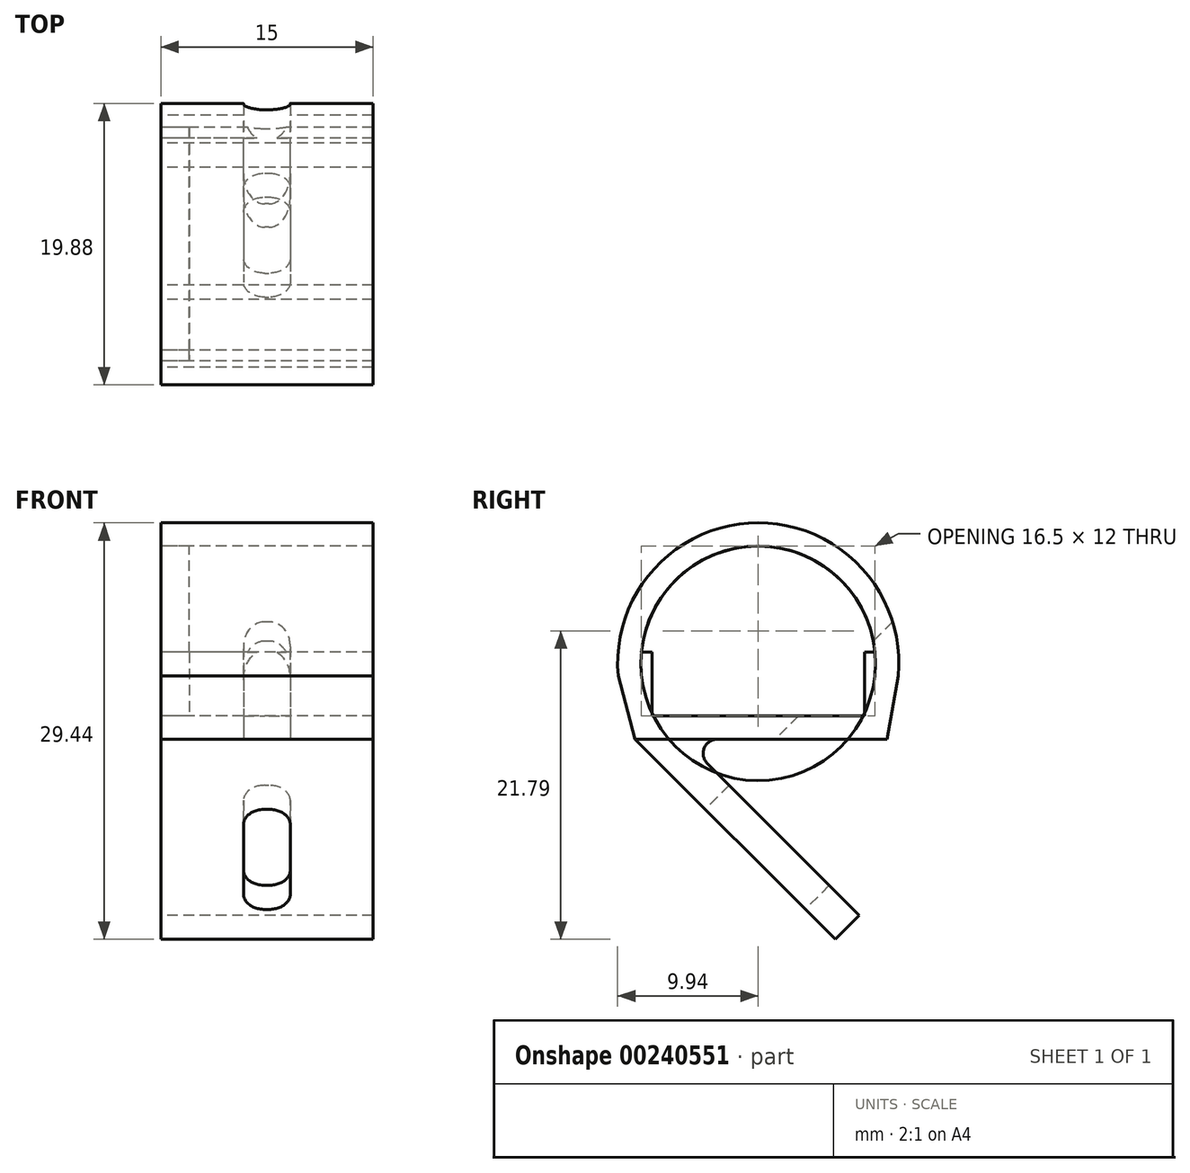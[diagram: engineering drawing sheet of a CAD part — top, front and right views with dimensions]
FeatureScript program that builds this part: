
annotation { "Feature Type Name" : "Feature", "Feature Type Description" : "" }
export const myFeature = defineFeature(function(context is Context, id is Id, definition is map)
    precondition{}
    {
        {
            var Q0;
            Q0=qCreatedBy(makeId("Right.planeOp"),FACE);
            var sketch = newSketch(context, id + "F0", { "sketchPlane" : qUnion([Q0])});
            skLineSegment(sketch, "E0.top", {"start": v(-7.5, -4.5) * mm, "end": v(7.5, -4.5) * mm});
            skLineSegment(sketch, "E0.left", {"start": v(-7.5, 0) * mm, "end": v(-7.5, -4.5) * mm});
            skLineSegment(sketch, "E0.right", {"start": v(7.5, 0) * mm, "end": v(7.5, -4.5) * mm});
            skLineSegment(sketch, "E1", {"start": v(-8.25, 0) * mm, "end": v(-7.5, 0) * mm});
            skArc(sketch, "E2", {"start": v(8.25, 0) * mm, "mid": v(0, 7.5) * mm, "end": v(-8.25, 0) * mm});
            skLineSegment(sketch, "E3", {"start": v(7.5, 0) * mm, "end": v(8.25, 0) * mm});
            skArc(sketch, "E4.3", {"start": v(9.9, -1.68) * mm, "mid": v(0, 9.15) * mm, "end": v(-9.9, -1.68) * mm});
            skLineSegment(sketch, "E4.4", {"start": v(-8.7, -6.15) * mm, "end": v(9.1, -6.15) * mm});
            skLineSegment(sketch, "E5", {"start": v(-9.9, -1.68) * mm, "end": v(-8.7, -6.15) * mm});
            skLineSegment(sketch, "E6", {"start": v(9.9, -1.68) * mm, "end": v(9.1, -6.15) * mm});
            skSolve(sketch);
        }
        {
            var Q0;
            Q0=makeQuery(id+"F0.imprint","IMPRINT",FACE,{"disambiguationData":[TD([[makeQuery(id+"F0.imprint","IMPRINT",EDGE,{"derivedFrom":sQuery(id+"F0.wireOp",EDGE,"E0.top")}),-1.0]])]});
            extrude(context, id + "F1", {"entities" : qUnion([Q0]), "depth" : 15 * mm});
        }
        {
            var Q0;
            Q0=makeQuery(id+"F0.imprint","IMPRINT",FACE,{"disambiguationData":[TD([[makeQuery(id+"F0.imprint","IMPRINT",EDGE,{"derivedFrom":sQuery(id+"F0.wireOp",EDGE,"E0.top")}),1.0]])]});
            extrude(context, id + "F2", {"entities" : qUnion([Q0]), "depth" : 2 * mm});
        }
        {
            var Q0;
            Q0=qCreatedBy(makeId("Right.planeOp"),FACE);
            var sketch = newSketch(context, id + "F3", { "sketchPlane" : qUnion([Q0])});
            skLineSegment(sketch, "E7.0", {"start": v(-2.9, -6.15) * mm, "end": v(9.1, -6.15) * mm});
            skLineSegment(sketch, "E8", {"start": v(-8.7, -6.15) * mm, "end": v(5.44, -20.3) * mm});
            skLineSegment(sketch, "E9", {"start": v(5.44, -20.3) * mm, "end": v(7.14, -18.6) * mm});
            skLineSegment(sketch, "E10", {"start": v(7.14, -18.6) * mm, "end": v(-3.6, -7.86) * mm});
            skPoint(sketch, "E11.newPointB", {"position": v(-8.7, -6.15) * mm});
            skArc(sketch, "E11.filletArc", {"start": v(-2.9, -6.15) * mm, "mid": v(-3.82, -6.77) * mm, "end": v(-3.6, -7.86) * mm});
            skLineSegment(sketch, "E12", {"start": v(-8.7, -6.15) * mm, "end": v(-2.9, -6.15) * mm});
            skSolve(sketch);
        }
        {
            var Q0;
            Q0=makeQuery(id+"F3.imprint","IMPRINT",FACE,{"disambiguationData":[TD([[makeQuery(id+"F3.imprint","IMPRINT",EDGE,{"derivedFrom":sQuery(id+"F3.wireOp",EDGE,"E8")}),1.0]])]});
            extrude(context, id + "F4", {"entities" : qUnion([Q0]), "depth" : 15 * mm});
        }
        {
            var Q0;
            Q0=makeQuery(id+"F4.opExtrude","SWEPT_FACE",FACE,{"disambiguationData":[OSD([sQuery(id+"F3.wireOp",EDGE,"E8")])]});
            var sketch = newSketch(context, id + "F5", { "sketchPlane" : qUnion([Q0])});
            skLineSegment(sketch, "E13.bottom", {"start": v(7.35, -15.2) * mm, "end": v(7.65, -15.2) * mm});
            skLineSegment(sketch, "E13.top", {"start": v(7.35, -5.2) * mm, "end": v(7.65, -5.2) * mm});
            skLineSegment(sketch, "E13.left", {"start": v(5.85, -13.7) * mm, "end": v(5.85, -6.7) * mm});
            skLineSegment(sketch, "E13.right", {"start": v(9.15, -13.7) * mm, "end": v(9.15, -6.7) * mm});
            skLineSegment(sketch, "E14.0.0", {"start": v(0, 1.8) * mm, "end": v(0, -18.2) * mm});
            skLineSegment(sketch, "E14.0.1", {"start": v(0, -18.2) * mm, "end": v(15, -18.2) * mm});
            skLineSegment(sketch, "E14.0.2", {"start": v(15, -18.2) * mm, "end": v(15, 1.8) * mm});
            skLineSegment(sketch, "E14.0.3", {"start": v(15, 1.8) * mm, "end": v(0, 1.8) * mm});
            skPoint(sketch, "E15.visualSharp", {"position": v(5.85, -15.2) * mm});
            skArc(sketch, "E15.filletArc", {"start": v(5.85, -13.7) * mm, "mid": v(6.29, -14.76) * mm, "end": v(7.35, -15.2) * mm});
            skPoint(sketch, "E16.visualSharp", {"position": v(9.15, -15.2) * mm});
            skArc(sketch, "E16.filletArc", {"start": v(7.65, -15.2) * mm, "mid": v(8.71, -14.76) * mm, "end": v(9.15, -13.7) * mm});
            skPoint(sketch, "E17.visualSharp", {"position": v(9.15, -5.2) * mm});
            skArc(sketch, "E17.filletArc", {"start": v(9.15, -6.7) * mm, "mid": v(8.71, -5.64) * mm, "end": v(7.65, -5.2) * mm});
            skPoint(sketch, "E18.visualSharp", {"position": v(5.85, -5.2) * mm});
            skArc(sketch, "E18.filletArc", {"start": v(7.35, -5.2) * mm, "mid": v(6.29, -5.64) * mm, "end": v(5.85, -6.7) * mm});
            skSolve(sketch);
        }
        {
            var Q0;
            Q0=makeQuery(id+"F5.imprint","IMPRINT",FACE,{"disambiguationData":[TD([[makeQuery(id+"F5.imprint","IMPRINT",EDGE,{"derivedFrom":sQuery(id+"F5.wireOp",EDGE,"E13.bottom")}),1.0]])]});
            extrude(context, id + "F6", {"entities" : qUnion([Q0]), "operationType" : NewBodyOperationType.REMOVE, "oppositeDirection" : true, "depth" : 25 * mm});
        }
        {
            var Q0;
            Q0=makeQuery(id+"F1.opExtrude","SWEPT_BODY",BODY,{"disambiguationData":[OSD([sQuery(id+"F0.wireOp",EDGE,"E0.top"),sQuery(id+"F0.wireOp",EDGE,"E0.left"),sQuery(id+"F0.wireOp",EDGE,"E0.right"),sQuery(id+"F0.wireOp",EDGE,"E1"),sQuery(id+"F0.wireOp",EDGE,"E2"),sQuery(id+"F0.wireOp",EDGE,"E3"),sQuery(id+"F0.wireOp",EDGE,"E4.3"),sQuery(id+"F0.wireOp",EDGE,"E4.4"),sQuery(id+"F0.wireOp",EDGE,"E5"),sQuery(id+"F0.wireOp",EDGE,"E6")])]});
            var Q1;
            Q1=qCreatedBy(makeId("Right.planeOp"),FACE);
            mirror(context, id + "F7", {"entities" : qUnion([Q0]), "mirrorPlane" : qUnion([Q1])});
        }
        {
            var Q0;
            Q0=makeQuery(id+"F7.opPattern","COPY",BODY,{"derivedFrom":makeQuery(id+"F1.opExtrude","SWEPT_BODY",BODY,{"disambiguationData":[OSD([sQuery(id+"F0.wireOp",EDGE,"E0.top"),sQuery(id+"F0.wireOp",EDGE,"E0.left"),sQuery(id+"F0.wireOp",EDGE,"E0.right"),sQuery(id+"F0.wireOp",EDGE,"E1"),sQuery(id+"F0.wireOp",EDGE,"E2"),sQuery(id+"F0.wireOp",EDGE,"E3"),sQuery(id+"F0.wireOp",EDGE,"E4.3"),sQuery(id+"F0.wireOp",EDGE,"E4.4"),sQuery(id+"F0.wireOp",EDGE,"E5"),sQuery(id+"F0.wireOp",EDGE,"E6")])]}),"instanceName":"1"});
            deleteBodies(context, id + "F8", {"entities" : qUnion([Q0])});
        }
    });
